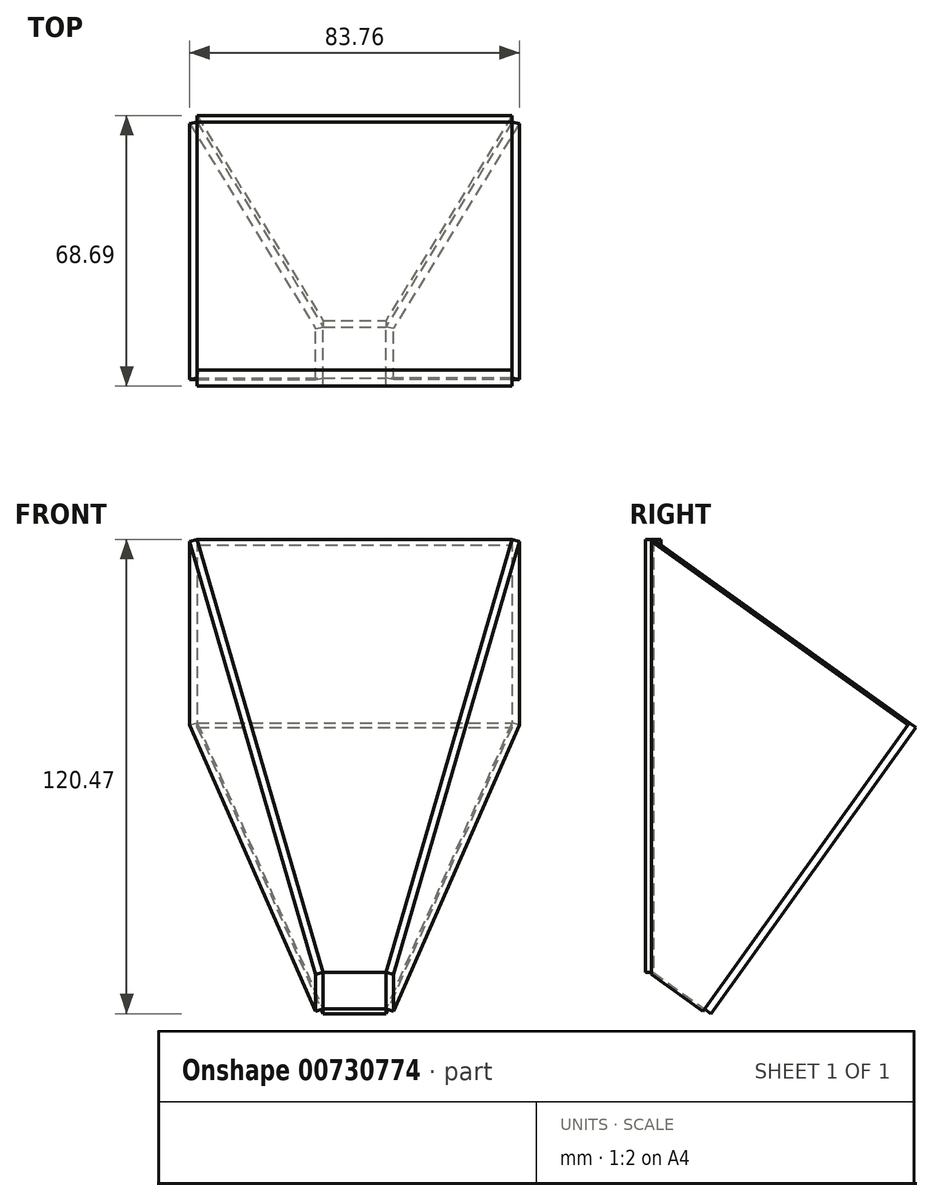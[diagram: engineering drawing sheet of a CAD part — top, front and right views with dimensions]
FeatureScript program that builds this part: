
annotation { "Feature Type Name" : "Feature", "Feature Type Description" : "" }
export const myFeature = defineFeature(function(context is Context, id is Id, definition is map)
    precondition{}
    {
        {
            assignVariable(context, id + "F0", {"name" : "wt", "anyValue" : 2});
        }
        {
            var Q0;
            Q0=qCreatedBy(makeId("Right.planeOp"),FACE);
            var sketch = newSketch(context, id + "F1", { "sketchPlane" : qUnion([Q0])});
            skLineSegment(sketch, "E0", {"start": v(0, 0) * mm, "end": v(0, -110) * mm});
            skLineSegment(sketch, "E1", {"start": v(0, -110) * mm, "end": v(13.01, -119.3) * mm});
            skLineSegment(sketch, "E2", {"start": v(13.01, -119.3) * mm, "end": v(65.07, -46.55) * mm});
            skLineSegment(sketch, "E3", {"start": v(65.07, -46.55) * mm, "end": v(0, 0) * mm});
            skSolve(sketch);
        }
        {
            var Q0;
            Q0=sQuery(id+"F1.wireOp",EDGE,"E3");
            cPlane(context, id + "F2", {"entities" : qUnion([Q0]), "cplaneType" : CPlaneType.LINE_ANGLE, "offset" : 25 * mm, "angle" : 0 * degree, "width" : 150 * mm, "height" : 150 * mm});
        }
        {
            var Q0;
            Q0=sQuery(id+"F1.wireOp",EDGE,"E1");
            cPlane(context, id + "F3", {"entities" : qUnion([Q0]), "cplaneType" : CPlaneType.LINE_ANGLE, "offset" : 25 * mm, "angle" : 0 * degree, "width" : 150 * mm, "height" : 150 * mm});
        }
        {
            var Q0;
            Q0=qCreatedBy(id+"F2.planeOp",FACE);
            var sketch = newSketch(context, id + "F4", { "sketchPlane" : qUnion([Q0])});
            skLineSegment(sketch, "E4", {"start": v(0, 0) * mm, "end": v(40, 0) * mm});
            skLineSegment(sketch, "E5.0", {"start": v(0, -80) * mm, "end": v(0, 0) * mm, "construction": true});
            skLineSegment(sketch, "E6", {"start": v(40, 0) * mm, "end": v(40, -80) * mm});
            skLineSegment(sketch, "E7", {"start": v(40, -80) * mm, "end": v(0, -80) * mm});
            skLineSegment(sketch, "E8.MirrorCS", {"start": v(0, 0) * mm, "end": v(-40, 0) * mm});
            skLineSegment(sketch, "E9.MirrorCS", {"start": v(-40, -80) * mm, "end": v(0, -80) * mm});
            skLineSegment(sketch, "E10.MirrorCS", {"start": v(-40, 0) * mm, "end": v(-40, -80) * mm});
            skSolve(sketch);
        }
        {
            var Q0;
            Q0=qCreatedBy(id+"F3.planeOp",FACE);
            var sketch = newSketch(context, id + "F5", { "sketchPlane" : qUnion([Q0])});
            skLineSegment(sketch, "E11.0", {"start": v(0, 64) * mm, "end": v(0, 80) * mm, "construction": true});
            skLineSegment(sketch, "E12", {"start": v(0, 64) * mm, "end": v(8, 64) * mm});
            skLineSegment(sketch, "E13", {"start": v(8, 64) * mm, "end": v(8, 80) * mm});
            skLineSegment(sketch, "E14", {"start": v(8, 80) * mm, "end": v(0, 80) * mm});
            skLineSegment(sketch, "E15.MirrorCS", {"start": v(0, 64) * mm, "end": v(-8, 64) * mm});
            skLineSegment(sketch, "E16.MirrorCS", {"start": v(-8, 64) * mm, "end": v(-8, 80) * mm});
            skLineSegment(sketch, "E17.MirrorCS", {"start": v(-8, 80) * mm, "end": v(0, 80) * mm});
            skSolve(sketch);
        }
        {
            var Q0;
            Q0=makeQuery(id+"F4.imprint","IMPRINT",FACE,{"disambiguationData":[TD([[makeQuery(id+"F4.imprint","IMPRINT",EDGE,{"derivedFrom":sQuery(id+"F4.wireOp",EDGE,"E4")}),-1.0]])]});
            var Q1;
            Q1=makeQuery(id+"F5.imprint","IMPRINT",FACE,{"disambiguationData":[TD([[makeQuery(id+"F5.imprint","IMPRINT",EDGE,{"derivedFrom":sQuery(id+"F5.wireOp",EDGE,"E12")}),1.0]])]});
            loft(context, id + "F6", {"sheetProfilesArray" : [{ "sheetProfileEntities" : qUnion([Q0]) }, { "sheetProfileEntities" : qUnion([Q1]) }]});
        }
        {
            var Q0;
            Q0=makeQuery(id+"F6.opLoft","SWEPT_FACE",FACE,{"disambiguationData":[OSD([sQuery(id+"F4.wireOp",EDGE,"E4"),sQuery(id+"F4.wireOp",EDGE,"E6"),sQuery(id+"F4.wireOp",EDGE,"E8.MirrorCS"),sQuery(id+"F5.wireOp",EDGE,"E12"),sQuery(id+"F5.wireOp",EDGE,"E13"),sQuery(id+"F5.wireOp",EDGE,"E15.MirrorCS")])]});
            var sketch = newSketch(context, id + "F7", { "sketchPlane" : qUnion([Q0])});
            skLineSegment(sketch, "E18.0", {"start": v(0, 0) * mm, "end": v(-40, 0) * mm});
            skLineSegment(sketch, "E18.1", {"start": v(0, 0) * mm, "end": v(40, 0) * mm});
            skLineSegment(sketch, "E18.2", {"start": v(40, 0) * mm, "end": v(8, -110) * mm});
            skLineSegment(sketch, "E18.3", {"start": v(-40, 0) * mm, "end": v(-8, -110) * mm});
            skLineSegment(sketch, "E18.4", {"start": v(8, -110) * mm, "end": v(-8, -110) * mm});
            skLineSegment(sketch, "E19", {"start": v(0, 0) * mm, "end": v(0, -110) * mm, "construction": true});
            skLineSegment(sketch, "E20", {"start": v(-31.27, -30) * mm, "end": v(31.27, -30) * mm});
            skCircle(sketch, "E21", {"center": v(-11, -15) * mm, "radius": 5 * mm});
            skLineSegment(sketch, "E22", {"start": v(-6, -15) * mm, "end": v(0, -15) * mm, "construction": true});
            skLineSegment(sketch, "E23", {"start": v(-7.43, -11.5) * mm, "end": v(0, -11.5) * mm});
            skLineSegment(sketch, "E24.MirrorCS", {"start": v(-7.43, -18.5) * mm, "end": v(0, -18.5) * mm});
            skLineSegment(sketch, "E25", {"start": v(0, -11.5) * mm, "end": v(0, 0) * mm});
            skLineSegment(sketch, "E26", {"start": v(0, -18.5) * mm, "end": v(0, -30) * mm});
            skCircle(sketch, "E27", {"center": v(-25.8, -7.8) * mm, "radius": 3.8 * mm});
            skLineSegment(sketch, "E28", {"start": v(-16, -15) * mm, "end": v(-35.64, -15) * mm, "construction": true});
            skCircle(sketch, "E29.MirrorC", {"center": v(-25.8, -22.2) * mm, "radius": 3.8 * mm});
            skCircle(sketch, "E30.MirrorC", {"center": v(25.8, -7.8) * mm, "radius": 3.8 * mm});
            skCircle(sketch, "E31.MirrorC", {"center": v(25.8, -22.2) * mm, "radius": 3.8 * mm});
            skLineSegment(sketch, "E32", {"start": v(-15.27, -85) * mm, "end": v(15.27, -85) * mm});
            skCircle(sketch, "E33", {"center": v(-5.5, -96.5) * mm, "radius": 3.5 * mm});
            skLineSegment(sketch, "E34", {"start": v(-2, -96.5) * mm, "end": v(0, -96.5) * mm, "construction": true});
            skLineSegment(sketch, "E35", {"start": v(-2.9, -94.15) * mm, "end": v(0, -94.15) * mm});
            skLineSegment(sketch, "E36.MirrorCS", {"start": v(-2.9, -98.85) * mm, "end": v(0, -98.85) * mm});
            skLineSegment(sketch, "E37", {"start": v(0, -94.15) * mm, "end": v(0, -85) * mm});
            skLineSegment(sketch, "E38", {"start": v(0, -98.85) * mm, "end": v(0, -110) * mm});
            skLineSegment(sketch, "E39", {"start": v(0, -85) * mm, "end": v(0, -30) * mm});
            skSolve(sketch);
        }
        {
            var Q0;
            {var subQ7=sQuery(id+"F7.wireOp",EDGE,"E18.1");Q0=makeQuery(id+"F7.imprint","IMPRINT",FACE,{"disambiguationData":[TD([[makeQuery(id+"F7.imprint","IMPRINT",EDGE,{"derivedFrom":subQ7}),1.0]])]});}
            var Q1;
            {var subQ0=sQuery(id+"F7.wireOp",EDGE,"E21");var subQ1=makeQuery(id+"F7.imprint","INTERSECT",VERTEX,{"derivedFrom":[subQ0,sQuery(id+"F7.wireOp",EDGE,"E23")]});Q1=makeQuery(id+"F7.imprint","IMPRINT",FACE,{"disambiguationData":[TD([[makeQuery(id+"F7.imprint","IMPRINT",EDGE,{"disambiguationData":[TD([[subQ1,-1.0]])],"derivedFrom":subQ0}),1.0]])]});}
            var Q2;
            {var subQ5=sQuery(id+"F7.wireOp",EDGE,"E39");Q2=makeQuery(id+"F7.imprint","IMPRINT",FACE,{"disambiguationData":[TD([[makeQuery(id+"F7.imprint","IMPRINT",EDGE,{"derivedFrom":subQ5}),-1.0]])]});}
            var Q3;
            {var subQ0=sQuery(id+"F7.wireOp",EDGE,"E35");Q3=makeQuery(id+"F7.imprint","IMPRINT",FACE,{"disambiguationData":[TD([[makeQuery(id+"F7.imprint","IMPRINT",EDGE,{"derivedFrom":subQ0}),-1.0]])]});}
            var Q4;
            {var subQ0=sQuery(id+"F7.wireOp",EDGE,"E33");var subQ1=makeQuery(id+"F7.imprint","INTERSECT",VERTEX,{"derivedFrom":[subQ0,sQuery(id+"F7.wireOp",EDGE,"E35")]});Q4=makeQuery(id+"F7.imprint","IMPRINT",FACE,{"disambiguationData":[TD([[makeQuery(id+"F7.imprint","IMPRINT",EDGE,{"disambiguationData":[TD([[subQ1,-1.0]])],"derivedFrom":subQ0}),1.0]])]});}
            extrude(context, id + "F8", {"entities" : qUnion([Q0, Q1, Q2, Q3, Q4]), "depth" : (getVariable(context, 'wt')) * mm, "offsetDistance" : 25 * mm});
        }
        {
            var Q0;
            {var subQ7=sQuery(id+"F7.wireOp",EDGE,"E18.0");Q0=makeQuery(id+"F7.imprint","IMPRINT",FACE,{"disambiguationData":[TD([[makeQuery(id+"F7.imprint","IMPRINT",EDGE,{"derivedFrom":subQ7}),1.0]])]});}
            var Q1;
            {var subQ5=sQuery(id+"F7.wireOp",EDGE,"E39");Q1=makeQuery(id+"F7.imprint","IMPRINT",FACE,{"disambiguationData":[TD([[makeQuery(id+"F7.imprint","IMPRINT",EDGE,{"derivedFrom":subQ5}),1.0]])]});}
            var Q2;
            {var subQ0=sQuery(id+"F7.wireOp",EDGE,"E35");Q2=makeQuery(id+"F7.imprint","IMPRINT",FACE,{"disambiguationData":[TD([[makeQuery(id+"F7.imprint","IMPRINT",EDGE,{"derivedFrom":subQ0}),1.0]])]});}
            extrude(context, id + "F9", {"entities" : qUnion([Q0, Q1, Q2]), "depth" : (getVariable(context, 'wt')) * mm, "offsetDistance" : 25 * mm});
        }
        {
            var Q0;
            Q0=makeQuery(id+"F6.opLoft","SWEPT_FACE",FACE,{"disambiguationData":[OSD([sQuery(id+"F4.wireOp",EDGE,"E4"),sQuery(id+"F4.wireOp",EDGE,"E6"),sQuery(id+"F4.wireOp",EDGE,"E7"),sQuery(id+"F5.wireOp",EDGE,"E12"),sQuery(id+"F5.wireOp",EDGE,"E13"),sQuery(id+"F5.wireOp",EDGE,"E14")])]});
            extrude(context, id + "F10", {"entities" : qUnion([Q0]), "depth" : (getVariable(context, 'wt')) * mm, "offsetDistance" : 25 * mm});
        }
        {
            var Q0;
            Q0=makeQuery(id+"F6.opLoft","SWEPT_FACE",FACE,{"disambiguationData":[OSD([sQuery(id+"F4.wireOp",EDGE,"E8.MirrorCS"),sQuery(id+"F4.wireOp",EDGE,"E9.MirrorCS"),sQuery(id+"F4.wireOp",EDGE,"E10.MirrorCS"),sQuery(id+"F5.wireOp",EDGE,"E15.MirrorCS"),sQuery(id+"F5.wireOp",EDGE,"E16.MirrorCS"),sQuery(id+"F5.wireOp",EDGE,"E17.MirrorCS")])]});
            extrude(context, id + "F11", {"entities" : qUnion([Q0]), "depth" : (getVariable(context, 'wt')) * mm, "offsetDistance" : 25 * mm});
        }
        {
            var Q0;
            Q0=makeQuery(id+"F6.opLoft","SWEPT_FACE",FACE,{"disambiguationData":[OSD([sQuery(id+"F4.wireOp",EDGE,"E7"),sQuery(id+"F4.wireOp",EDGE,"E9.MirrorCS"),sQuery(id+"F4.wireOp",EDGE,"E10.MirrorCS"),sQuery(id+"F5.wireOp",EDGE,"E14"),sQuery(id+"F5.wireOp",EDGE,"E16.MirrorCS"),sQuery(id+"F5.wireOp",EDGE,"E17.MirrorCS")])]});
            extrude(context, id + "F12", {"entities" : qUnion([Q0]), "depth" : (getVariable(context, 'wt')) * mm, "offsetDistance" : 25 * mm});
        }
        {
            var Q0;
            Q0=makeQuery(id+"F6.opLoft","SWEPT_FACE",FACE,{"disambiguationData":[OSD([sQuery(id+"F4.wireOp",EDGE,"E4"),sQuery(id+"F4.wireOp",EDGE,"E6"),sQuery(id+"F4.wireOp",EDGE,"E8.MirrorCS"),sQuery(id+"F5.wireOp",EDGE,"E12"),sQuery(id+"F5.wireOp",EDGE,"E13"),sQuery(id+"F5.wireOp",EDGE,"E15.MirrorCS")])]});
            extrude(context, id + "F13", {"entities" : qUnion([Q0]), "oppositeDirection" : true, "depth" : (getVariable(context, 'wt')) * mm, "offsetDistance" : 25 * mm});
        }
        {
            var Q0;
            Q0=makeQuery(id+"F6.opLoft","SWEPT_FACE",FACE,{"disambiguationData":[OSD([sQuery(id+"F4.wireOp",EDGE,"E4"),sQuery(id+"F4.wireOp",EDGE,"E6"),sQuery(id+"F4.wireOp",EDGE,"E8.MirrorCS"),sQuery(id+"F5.wireOp",EDGE,"E12"),sQuery(id+"F5.wireOp",EDGE,"E13"),sQuery(id+"F5.wireOp",EDGE,"E15.MirrorCS")])]});
            extrude(context, id + "F14", {"entities" : qUnion([Q0]), "operationType" : NewBodyOperationType.ADD, "depth" : (getVariable(context, 'wt')) * mm, "offsetDistance" : 25 * mm});
        }
    });
